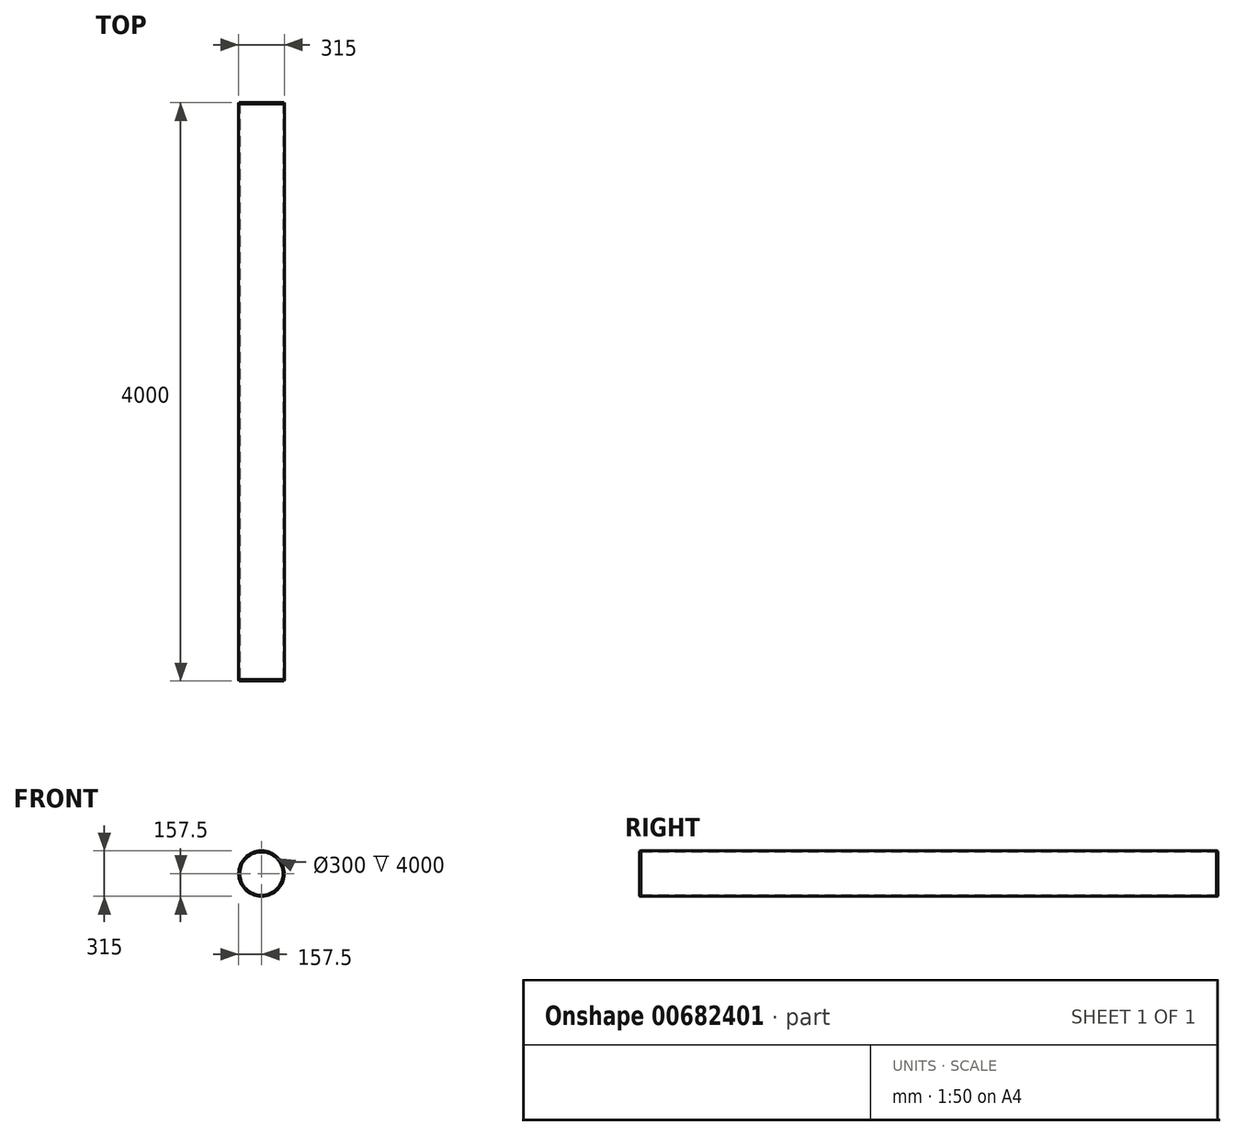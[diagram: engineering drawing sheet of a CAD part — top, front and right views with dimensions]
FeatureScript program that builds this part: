
annotation { "Feature Type Name" : "Feature", "Feature Type Description" : "" }
export const myFeature = defineFeature(function(context is Context, id is Id, definition is map)
    precondition{}
    {
        {
            var Q0;
            Q0=qCreatedBy(makeId("Front.planeOp"),FACE);
            var sketch = newSketch(context, id + "F0", { "sketchPlane" : qUnion([Q0])});
            skCircle(sketch, "E0", {"center": v(0, 0) * mm, "radius": 157.5 * mm});
            skSolve(sketch);
        }
        {
            var Q0;
            Q0=makeQuery(id+"F0.imprint","IMPRINT",FACE,{"disambiguationData":[TD([[makeQuery(id+"F0.imprint","IMPRINT",EDGE,{"derivedFrom":sQuery(id+"F0.wireOp",EDGE,"E0")}),1.0]])]});
            extrude(context, id + "F1", {"entities" : qUnion([Q0]), "depth" : 4000 * mm, "offsetDistance" : 25 * mm});
        }
        {
            var Q0;
            Q0=makeQuery(id+"F1.opExtrude","CAP_FACE",FACE,{"disambiguationData":[OSD([sQuery(id+"F0.wireOp",EDGE,"E0")])],"isStart":false});
            var sketch = newSketch(context, id + "F2", { "sketchPlane" : qUnion([Q0])});
            skCircle(sketch, "E1", {"center": v(0, 0) * mm, "radius": 150 * mm});
            skSolve(sketch);
        }
        {
            var Q0;
            Q0=makeQuery(id+"F2.imprint","IMPRINT",FACE,{"disambiguationData":[TD([[makeQuery(id+"F2.imprint","IMPRINT",EDGE,{"derivedFrom":sQuery(id+"F2.wireOp",EDGE,"E1")}),1.0]])]});
            extrude(context, id + "F3", {"entities" : qUnion([Q0]), "operationType" : NewBodyOperationType.REMOVE, "endBound" : BoundingType.THROUGH_ALL, "oppositeDirection" : true, "depth" : 25 * mm, "offsetDistance" : 25 * mm});
        }
        {
            var Q0;
            Q0=makeQuery(id+"F1.opExtrude","CAP_EDGE",EDGE,{"disambiguationData":[OSD([sQuery(id+"F0.wireOp",EDGE,"E0")])],"isStart":false});
            chamfer(context, id + "F4", {"entities" : qUnion([Q0]), "chamferType" : ChamferType.TWO_OFFSETS, "width1" : 2.5 * mm, "oppositeDirection" : false, "width2" : 10 * mm, "tangentPropagation" : true});
        }
        {
            var Q0;
            Q0=makeQuery(id+"F1.opExtrude","CAP_EDGE",EDGE,{"disambiguationData":[OSD([sQuery(id+"F0.wireOp",EDGE,"E0")])],"isStart":true});
            chamfer(context, id + "F5", {"entities" : qUnion([Q0]), "chamferType" : ChamferType.TWO_OFFSETS, "width1" : 2.5 * mm, "oppositeDirection" : true, "width2" : 10 * mm, "tangentPropagation" : true});
        }
    });
